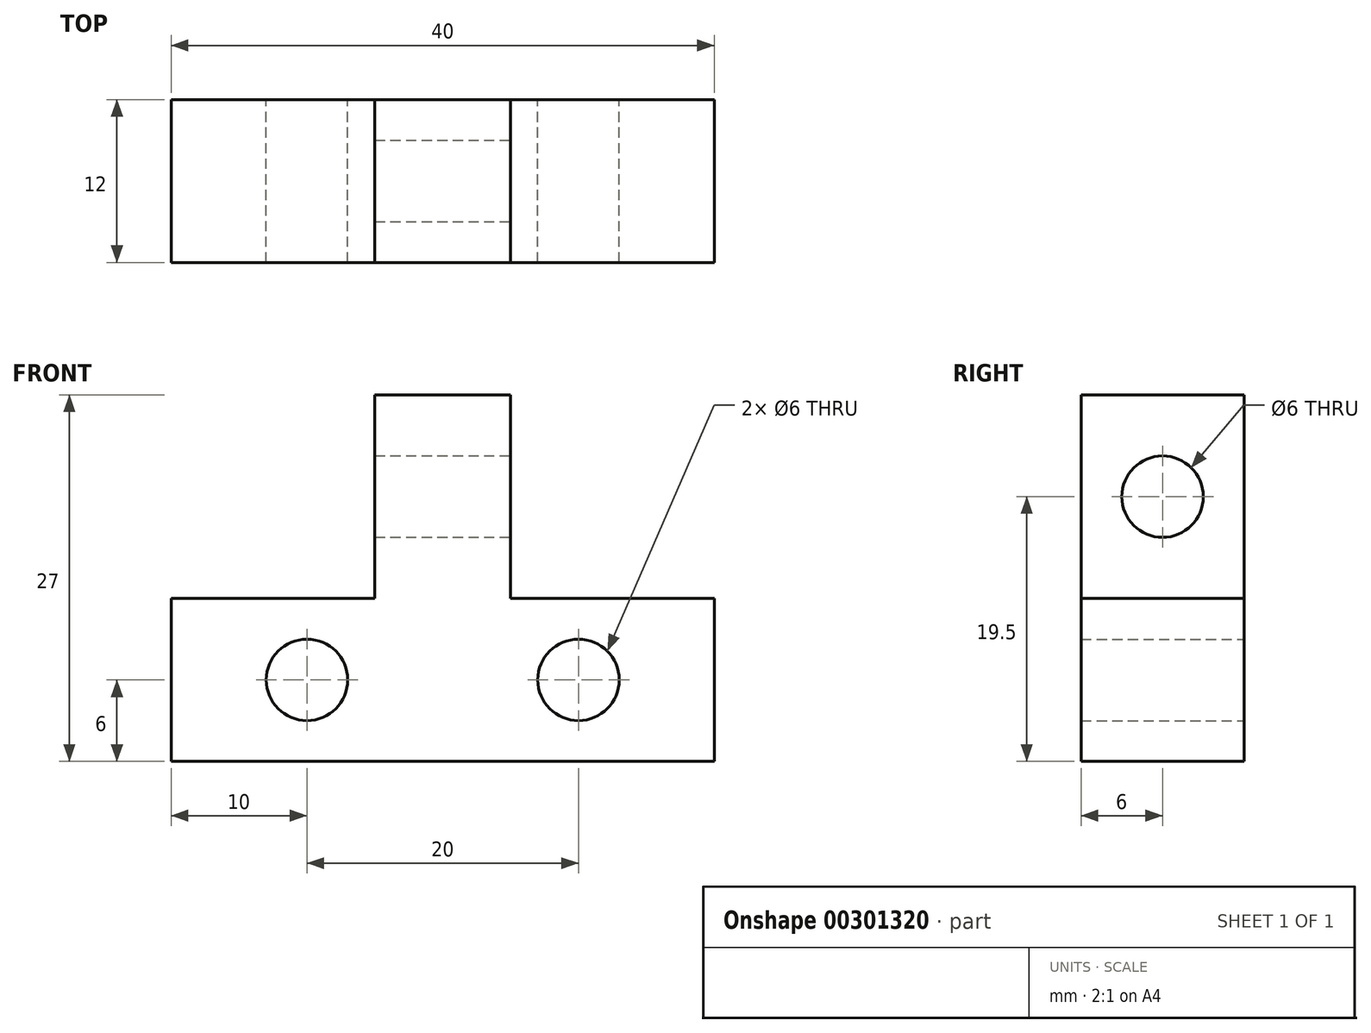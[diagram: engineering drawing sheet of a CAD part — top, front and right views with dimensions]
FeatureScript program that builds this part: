
annotation { "Feature Type Name" : "Feature", "Feature Type Description" : "" }
export const myFeature = defineFeature(function(context is Context, id is Id, definition is map)
    precondition{}
    {
        {
            var Q0;
            Q0=qCreatedBy(makeId("Front.planeOp"),FACE);
            var sketch = newSketch(context, id + "F0", { "sketchPlane" : qUnion([Q0])});
            skLineSegment(sketch, "E0.bottom", {"start": v(0, 0) * mm, "end": v(40, 0) * mm});
            skLineSegment(sketch, "E0.top", {"start": v(0, 12) * mm, "end": v(40, 12) * mm});
            skLineSegment(sketch, "E0.left", {"start": v(0, 0) * mm, "end": v(0, 12) * mm});
            skLineSegment(sketch, "E0.right", {"start": v(40, 0) * mm, "end": v(40, 12) * mm});
            skLineSegment(sketch, "E1.bottom", {"start": v(15, 12) * mm, "end": v(25, 12) * mm});
            skLineSegment(sketch, "E1.top", {"start": v(15, 27) * mm, "end": v(25, 27) * mm});
            skLineSegment(sketch, "E1.left", {"start": v(15, 12) * mm, "end": v(15, 27) * mm});
            skLineSegment(sketch, "E1.right", {"start": v(25, 12) * mm, "end": v(25, 27) * mm});
            skPoint(sketch, "E2", {"position": v(20, 27) * mm});
            skPoint(sketch, "E3", {"position": v(20, 12) * mm});
            skCircle(sketch, "E4", {"center": v(10, 6) * mm, "radius": 3 * mm});
            skCircle(sketch, "E5", {"center": v(30, 6) * mm, "radius": 3 * mm});
            skLineSegment(sketch, "E6", {"start": v(10, 6) * mm, "end": v(30, 6) * mm});
            skPoint(sketch, "E7", {"position": v(20, 6) * mm});
            skPoint(sketch, "E8", {"position": v(40, 6) * mm});
            skSolve(sketch);
        }
        {
            var Q0;
            Q0=qSketchRegion(id+"F0",true);
            extrude(context, id + "F1", {"entities" : qUnion([Q0]), "depth" : 12 * mm});
        }
        {
            var Q0;
            Q0=makeQuery(id+"F1.opExtrude","SWEPT_FACE",FACE,{"disambiguationData":[OSD([sQuery(id+"F0.wireOp",EDGE,"E1.right")])]});
            var sketch = newSketch(context, id + "F2", { "sketchPlane" : qUnion([Q0])});
            skCircle(sketch, "E9", {"center": v(-6, 19.5) * mm, "radius": 3 * mm});
            skPoint(sketch, "E10", {"position": v(-12, 19.5) * mm});
            skPoint(sketch, "E11", {"position": v(-6, 27) * mm});
            skSolve(sketch);
        }
        {
            var Q0;
            Q0 = qSketchRegion(id + "F2", true);
            extrude(context, id + "F3", {"entities" : qUnion([Q0]), "operationType" : NewBodyOperationType.REMOVE, "oppositeDirection" : true, "depth" : 25 * mm});
        }
    });
